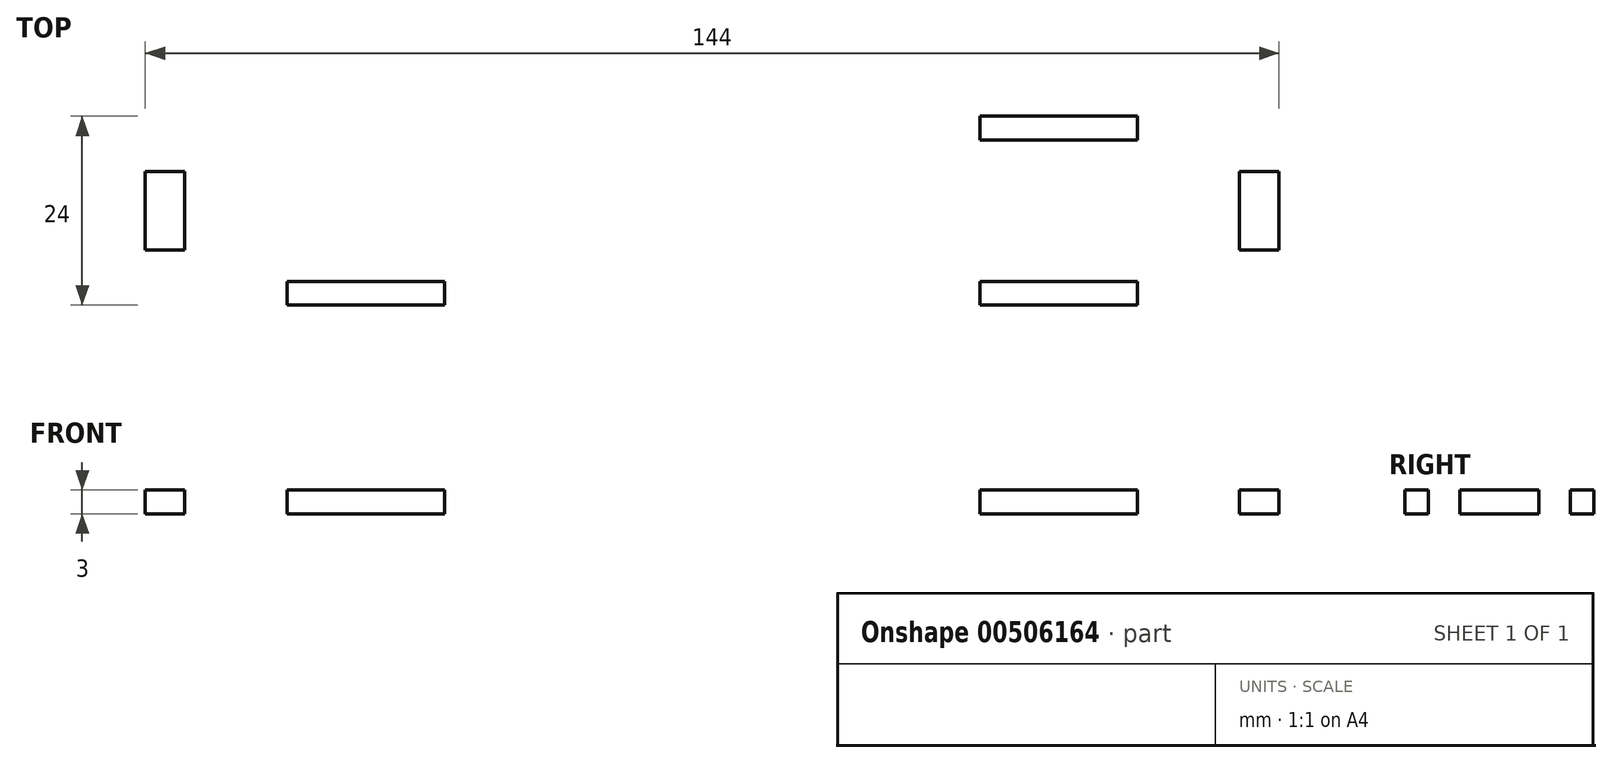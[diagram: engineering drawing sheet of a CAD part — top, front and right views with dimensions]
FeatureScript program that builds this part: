
annotation { "Feature Type Name" : "Feature", "Feature Type Description" : "" }
export const myFeature = defineFeature(function(context is Context, id is Id, definition is map)
    precondition{}
    {
        {
            var Q0;
            Q0=qCreatedBy(makeId("Top.planeOp"),FACE);
            var sketch = newSketch(context, id + "F0", { "sketchPlane" : qUnion([Q0])});
            skLineSegment(sketch, "E0.bottom", {"start": v(67, -9) * mm, "end": v(-67, -9) * mm});
            skLineSegment(sketch, "E0.top", {"start": v(67, 9) * mm, "end": v(-67, 9) * mm});
            skLineSegment(sketch, "E0.left", {"start": v(67, -9) * mm, "end": v(67, 9) * mm});
            skLineSegment(sketch, "E0.right", {"start": v(-67, -9) * mm, "end": v(-67, 9) * mm});
            skPoint(sketch, "E0.middle", {"position": v(0, 0) * mm});
            skLineSegment(sketch, "E1.bottom", {"start": v(-54, 9) * mm, "end": v(-34, 9) * mm});
            skLineSegment(sketch, "E1.top", {"start": v(-54, 12) * mm, "end": v(-34, 12) * mm});
            skLineSegment(sketch, "E1.left", {"start": v(-54, 9) * mm, "end": v(-54, 12) * mm});
            skLineSegment(sketch, "E1.right", {"start": v(-34, 9) * mm, "end": v(-34, 12) * mm});
            skLineSegment(sketch, "E2.bottom", {"start": v(-67, 5) * mm, "end": v(-72, 5) * mm});
            skLineSegment(sketch, "E2.top", {"start": v(-67, -5) * mm, "end": v(-72, -5) * mm});
            skLineSegment(sketch, "E2.left", {"start": v(-67, 5) * mm, "end": v(-67, -5) * mm});
            skLineSegment(sketch, "E2.right", {"start": v(-72, 5) * mm, "end": v(-72, -5) * mm});
            skLineSegment(sketch, "E3", {"start": v(0, 0) * mm, "end": v(0, 6.42) * mm, "construction": true});
            skLineSegment(sketch, "E4", {"start": v(-6.88, 0) * mm, "end": v(6.85, 0) * mm, "construction": true});
            skLineSegment(sketch, "E5.MirrorCS", {"start": v(54, 9) * mm, "end": v(54, 12) * mm});
            skLineSegment(sketch, "E6.MirrorCS", {"start": v(54, 12) * mm, "end": v(34, 12) * mm});
            skLineSegment(sketch, "E7.MirrorCS", {"start": v(34, 9) * mm, "end": v(34, 12) * mm});
            skLineSegment(sketch, "E8.MirrorCS", {"start": v(67, 5) * mm, "end": v(72, 5) * mm});
            skLineSegment(sketch, "E9.MirrorCS", {"start": v(72, 5) * mm, "end": v(72, -5) * mm});
            skLineSegment(sketch, "E10.MirrorCS", {"start": v(67, -5) * mm, "end": v(72, -5) * mm});
            skLineSegment(sketch, "E11.MirrorCS", {"start": v(-34, -9) * mm, "end": v(-34, -12) * mm});
            skLineSegment(sketch, "E12.MirrorCS", {"start": v(-54, -12) * mm, "end": v(-34, -12) * mm});
            skLineSegment(sketch, "E13.MirrorCS", {"start": v(-54, -9) * mm, "end": v(-54, -12) * mm});
            skLineSegment(sketch, "E14.MirrorCS", {"start": v(54, -12) * mm, "end": v(34, -12) * mm});
            skLineSegment(sketch, "E15.MirrorCS", {"start": v(34, -9) * mm, "end": v(34, -12) * mm});
            skLineSegment(sketch, "E16.MirrorCS", {"start": v(54, -9) * mm, "end": v(54, -12) * mm});
            skSolve(sketch);
        }
        {
            var Q0;
            Q0=makeQuery(id+"F0.imprint","IMPRINT",FACE,{"disambiguationData":[TD([[makeQuery(id+"F0.imprint","IMPRINT",EDGE,{"derivedFrom":sQuery(id+"F0.wireOp",EDGE,"E1.bottom")}),1.0]])]});
            var Q1;
            Q1=makeQuery(id+"F0.imprint","IMPRINT",FACE,{"disambiguationData":[TD([[makeQuery(id+"F0.imprint","IMPRINT",EDGE,{"derivedFrom":sQuery(id+"F0.wireOp",EDGE,"E14.MirrorCS")}),-1.0]])]});
            var Q2;
            {var subQ0=sQuery(id+"F0.wireOp",EDGE,"E8.MirrorCS");Q2=makeQuery(id+"F0.imprint","IMPRINT",FACE,{"disambiguationData":[TD([[makeQuery(id+"F0.imprint","IMPRINT",EDGE,{"derivedFrom":subQ0}),-1.0]])]});}
            var Q3;
            {var subQ0=sQuery(id+"F0.wireOp",EDGE,"E11.MirrorCS");Q3=makeQuery(id+"F0.imprint","IMPRINT",FACE,{"disambiguationData":[TD([[makeQuery(id+"F0.imprint","IMPRINT",EDGE,{"derivedFrom":subQ0}),-1.0]])]});}
            var Q4;
            {var subQ0=sQuery(id+"F0.wireOp",EDGE,"E5.MirrorCS");Q4=makeQuery(id+"F0.imprint","IMPRINT",FACE,{"disambiguationData":[TD([[makeQuery(id+"F0.imprint","IMPRINT",EDGE,{"derivedFrom":subQ0}),1.0]])]});}
            var Q5;
            Q5=makeQuery(id+"F0.imprint","IMPRINT",FACE,{"disambiguationData":[TD([[makeQuery(id+"F0.imprint","IMPRINT",EDGE,{"derivedFrom":sQuery(id+"F0.wireOp",EDGE,"E2.bottom")}),1.0]])]});
            var Q6;
            {var subQ7=sQuery(id+"F0.wireOp",EDGE,"E1.bottom");Q6=makeQuery(id+"F0.imprint","IMPRINT",FACE,{"disambiguationData":[TD([[makeQuery(id+"F0.imprint","IMPRINT",EDGE,{"derivedFrom":subQ7}),-1.0]])]});}
            extrude(context, id + "F1", {"entities" : qUnion([Q0, Q1, Q2, Q3, Q4, Q5, Q6]), "depth" : 3 * mm});
        }
    });
